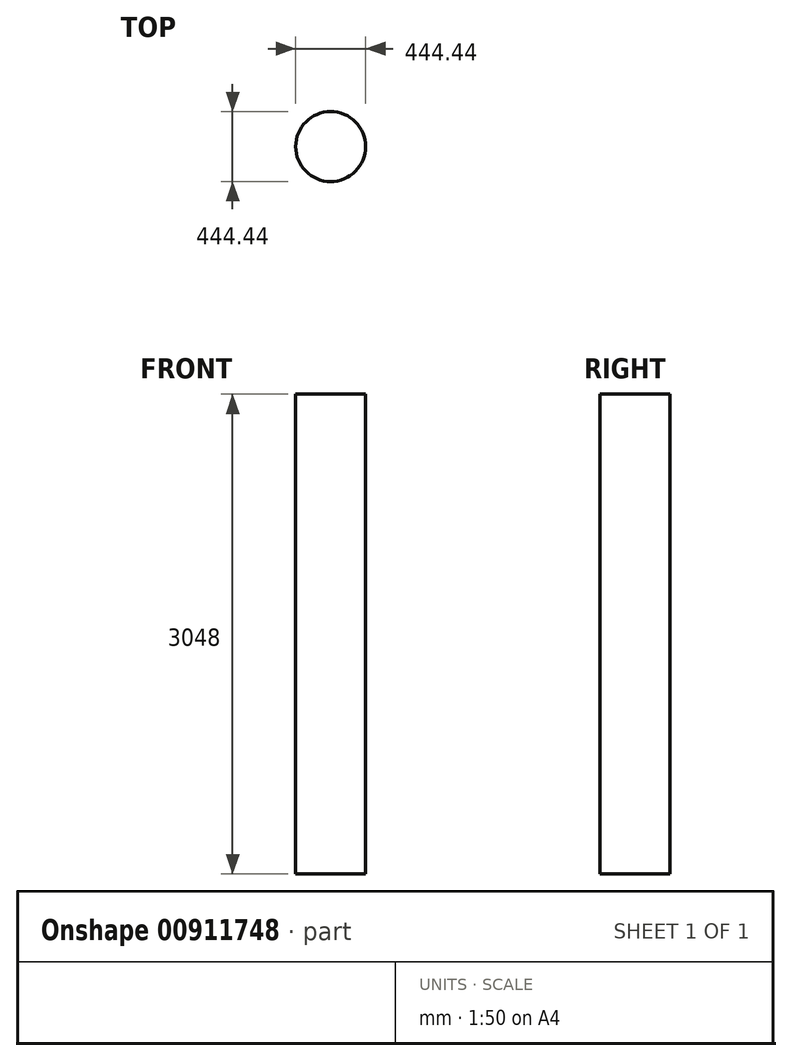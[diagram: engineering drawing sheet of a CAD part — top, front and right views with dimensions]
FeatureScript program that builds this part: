
annotation { "Feature Type Name" : "Feature", "Feature Type Description" : "" }
export const myFeature = defineFeature(function(context is Context, id is Id, definition is map)
    precondition{}
    {
        {
            var Q0;
            Q0=qCreatedBy(makeId("Top.planeOp"),FACE);
            var Q1;
            Q1=qCreatedBy(makeId("Top.planeOp"),FACE);
            var sketch = newSketch(context, id + "F0", { "sketchPlane" : qUnion([Q0, Q1])});
            skCircle(sketch, "E0", {"center": v(0, 0) * mm, "radius": 222.22 * mm});
            skSolve(sketch);
        }
        {
            var Q0;
            Q0=makeQuery(id+"F0.imprint","IMPRINT",FACE,{"disambiguationData":[TD([[makeQuery(id+"F0.imprint","IMPRINT",EDGE,{"derivedFrom":sQuery(id+"F0.wireOp",EDGE,"E0")}),1.0]])]});
            extrude(context, id + "F1", {"entities" : qUnion([Q0]), "oppositeDirection" : true, "depth" : 3048 * mm, "offsetDistance" : 25.4 * mm});
        }
    });
